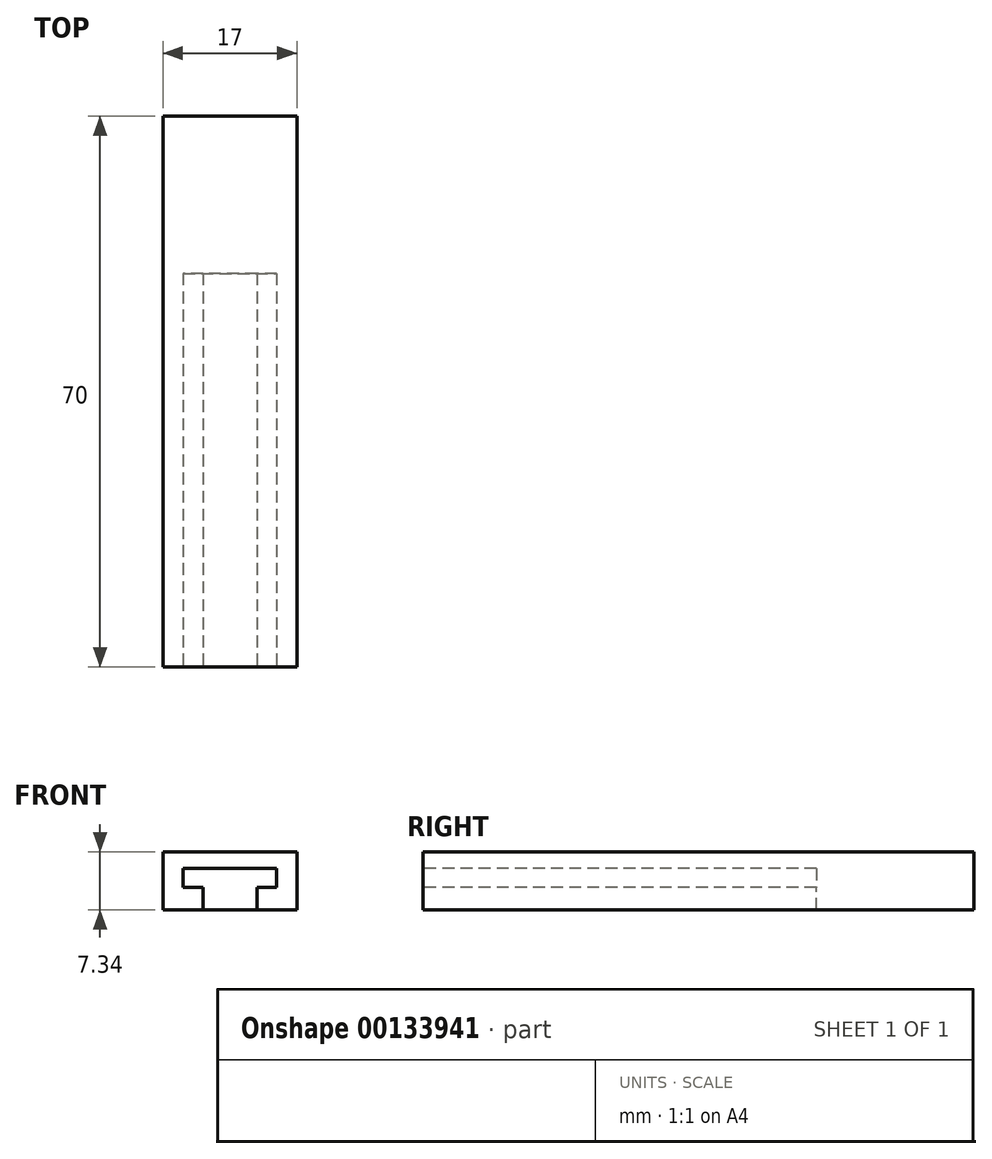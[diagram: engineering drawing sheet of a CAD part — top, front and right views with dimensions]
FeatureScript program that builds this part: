
annotation { "Feature Type Name" : "Feature", "Feature Type Description" : "" }
export const myFeature = defineFeature(function(context is Context, id is Id, definition is map)
    precondition{}
    {
        {
            var Q0;
            Q0=qCreatedBy(makeId("Front.planeOp"),FACE);
            var sketch = newSketch(context, id + "F0", { "sketchPlane" : qUnion([Q0])});
            skLineSegment(sketch, "E0.bottom", {"start": v(8.5, -3.68) * mm, "end": v(-8.5, -3.68) * mm});
            skLineSegment(sketch, "E0.top", {"start": v(8.5, 3.67) * mm, "end": v(-8.5, 3.67) * mm});
            skLineSegment(sketch, "E0.left", {"start": v(8.5, -3.68) * mm, "end": v(8.5, 3.67) * mm});
            skLineSegment(sketch, "E0.right", {"start": v(-8.5, -3.68) * mm, "end": v(-8.5, 3.67) * mm});
            skPoint(sketch, "E0.middle", {"position": v(0, 0) * mm});
            skSolve(sketch);
        }
        {
            var Q0;
            Q0 = qSketchRegion(id + "F0", true);
            extrude(context, id + "F1", {"entities" : qUnion([Q0]), "oppositeDirection" : true, "depth" : 70 * mm});
        }
        {
            var Q0;
            Q0=makeQuery(id+"F1.opExtrude","CAP_FACE",FACE,{"disambiguationData":[OSD([sQuery(id+"F0.wireOp",EDGE,"E0.bottom"),sQuery(id+"F0.wireOp",EDGE,"E0.top"),sQuery(id+"F0.wireOp",EDGE,"E0.left"),sQuery(id+"F0.wireOp",EDGE,"E0.right")])],"isStart":true});
            var sketch = newSketch(context, id + "F2", { "sketchPlane" : qUnion([Q0])});
            skLineSegment(sketch, "E1", {"start": v(-3.43, -3.68) * mm, "end": v(-3.43, -0.83) * mm});
            skLineSegment(sketch, "E2", {"start": v(-3.43, -0.83) * mm, "end": v(-5.93, -0.83) * mm});
            skLineSegment(sketch, "E3", {"start": v(-5.93, -0.83) * mm, "end": v(-5.93, 1.57) * mm});
            skLineSegment(sketch, "E4", {"start": v(-5.93, 1.57) * mm, "end": v(5.93, 1.57) * mm});
            skLineSegment(sketch, "E5", {"start": v(5.93, 1.57) * mm, "end": v(5.93, -0.83) * mm});
            skLineSegment(sketch, "E6", {"start": v(5.93, -0.83) * mm, "end": v(3.43, -0.83) * mm});
            skLineSegment(sketch, "E7", {"start": v(3.43, -0.83) * mm, "end": v(3.43, -3.68) * mm});
            skLineSegment(sketch, "E8", {"start": v(-3.43, -3.68) * mm, "end": v(3.43, -3.68) * mm});
            skSolve(sketch);
        }
        {
            var Q0;
            Q0 = qSketchRegion(id + "F2", true);
            extrude(context, id + "F3", {"entities" : qUnion([Q0]), "operationType" : NewBodyOperationType.REMOVE, "oppositeDirection" : true, "depth" : 50 * mm});
        }
    });
